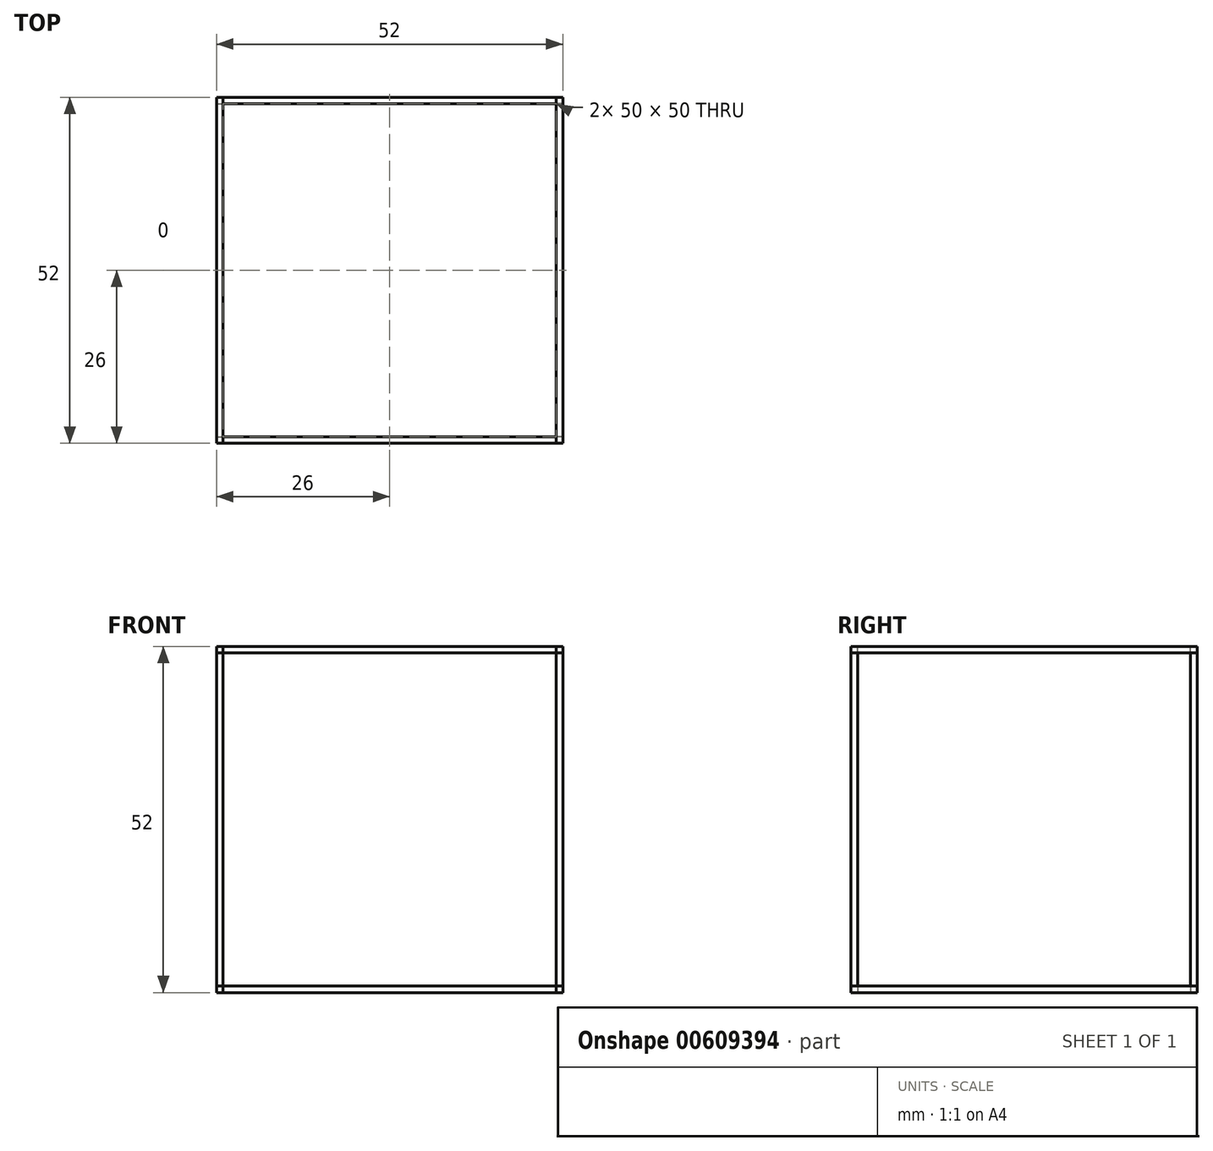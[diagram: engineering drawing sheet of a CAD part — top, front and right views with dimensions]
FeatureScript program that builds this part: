
annotation { "Feature Type Name" : "Feature", "Feature Type Description" : "" }
export const myFeature = defineFeature(function(context is Context, id is Id, definition is map)
    precondition{}
    {
        {
            var Q0;
            Q0=qCreatedBy(makeId("Top.planeOp"),FACE);
            var sketch = newSketch(context, id + "F0", { "sketchPlane" : qUnion([Q0])});
            skLineSegment(sketch, "E0.bottom", {"start": v(25, -25) * mm, "end": v(-25, -25) * mm});
            skLineSegment(sketch, "E0.top", {"start": v(25, 25) * mm, "end": v(-25, 25) * mm});
            skLineSegment(sketch, "E0.left", {"start": v(25, -25) * mm, "end": v(25, 25) * mm});
            skLineSegment(sketch, "E0.right", {"start": v(-25, -25) * mm, "end": v(-25, 25) * mm});
            skPoint(sketch, "E0.middle", {"position": v(0, 0) * mm});
            skLineSegment(sketch, "E1.0", {"start": v(26, 26) * mm, "end": v(-26, 26) * mm});
            skLineSegment(sketch, "E1.1", {"start": v(26, -26) * mm, "end": v(26, 26) * mm});
            skLineSegment(sketch, "E1.2", {"start": v(26, -26) * mm, "end": v(-26, -26) * mm});
            skLineSegment(sketch, "E1.3", {"start": v(-26, -26) * mm, "end": v(-26, 26) * mm});
            skSolve(sketch);
        }
        {
            var Q0;
            Q0 = qSketchRegion(id + "F0", true);
            extrude(context, id + "F1", {"entities" : qUnion([Q0]), "depth" : 1 * mm, "offsetDistance" : 25 * mm});
        }
        {
            var Q0;
            Q0=makeQuery(id+"F1.opExtrude","SWEPT_BODY",BODY,{"disambiguationData":[OSD([sQuery(id+"F0.wireOp",EDGE,"E0.bottom"),sQuery(id+"F0.wireOp",EDGE,"E0.top"),sQuery(id+"F0.wireOp",EDGE,"E0.left"),sQuery(id+"F0.wireOp",EDGE,"E0.right"),sQuery(id+"F0.wireOp",EDGE,"E1.0"),sQuery(id+"F0.wireOp",EDGE,"E1.1"),sQuery(id+"F0.wireOp",EDGE,"E1.2"),sQuery(id+"F0.wireOp",EDGE,"E1.3")])]});
            var Q1;
            Q1=makeQuery(id+"F1.opExtrude","CAP_EDGE",EDGE,{"disambiguationData":[OSD([sQuery(id+"F0.wireOp",EDGE,"E1.3")])],"isStart":false});
            transform(context, id + "F2", {"entities" : qUnion([Q0]), "transformType" : TransformType.ROTATION, "transformAxis" : qUnion([Q1]), "angle" : 90 * degree, "oppositeDirection" : true, "makeCopy" : true});
        }
        {
            var Q0;
            Q0=makeQuery(id+"F2.opPattern","COPY",BODY,{"derivedFrom":makeQuery(id+"F1.opExtrude","SWEPT_BODY",BODY,{"disambiguationData":[OSD([sQuery(id+"F0.wireOp",EDGE,"E0.bottom"),sQuery(id+"F0.wireOp",EDGE,"E0.top"),sQuery(id+"F0.wireOp",EDGE,"E0.left"),sQuery(id+"F0.wireOp",EDGE,"E0.right"),sQuery(id+"F0.wireOp",EDGE,"E1.0"),sQuery(id+"F0.wireOp",EDGE,"E1.1"),sQuery(id+"F0.wireOp",EDGE,"E1.2"),sQuery(id+"F0.wireOp",EDGE,"E1.3")])]}),"instanceName":"1"});
            var Q1;
            Q1=makeQuery(id+"F2.opPattern","COPY",EDGE,{"derivedFrom":makeQuery(id+"F1.opExtrude","CAP_EDGE",EDGE,{"disambiguationData":[OSD([sQuery(id+"F0.wireOp",EDGE,"E1.1")])],"isStart":false}),"instanceName":"1"});
            transform(context, id + "F3", {"entities" : qUnion([Q0]), "transformType" : TransformType.ROTATION, "transformAxis" : qUnion([Q1]), "angle" : 90 * degree, "oppositeDirection" : true, "makeCopy" : true});
        }
        {
            var Q0;
            Q0=makeQuery(id+"F3.opPattern","COPY",BODY,{"derivedFrom":makeQuery(id+"F2.opPattern","COPY",BODY,{"derivedFrom":makeQuery(id+"F1.opExtrude","SWEPT_BODY",BODY,{"disambiguationData":[OSD([sQuery(id+"F0.wireOp",EDGE,"E0.bottom"),sQuery(id+"F0.wireOp",EDGE,"E0.top"),sQuery(id+"F0.wireOp",EDGE,"E0.left"),sQuery(id+"F0.wireOp",EDGE,"E0.right"),sQuery(id+"F0.wireOp",EDGE,"E1.0"),sQuery(id+"F0.wireOp",EDGE,"E1.1"),sQuery(id+"F0.wireOp",EDGE,"E1.2"),sQuery(id+"F0.wireOp",EDGE,"E1.3")])]}),"instanceName":"1"}),"instanceName":"1"});
            var Q1;
            Q1=makeQuery(id+"F3.opPattern","COPY",EDGE,{"derivedFrom":makeQuery(id+"F2.opPattern","COPY",EDGE,{"derivedFrom":makeQuery(id+"F1.opExtrude","CAP_EDGE",EDGE,{"disambiguationData":[OSD([sQuery(id+"F0.wireOp",EDGE,"E1.3")])],"isStart":false}),"instanceName":"1"}),"instanceName":"1"});
            transform(context, id + "F4", {"entities" : qUnion([Q0]), "transformType" : TransformType.ROTATION, "transformAxis" : qUnion([Q1]), "angle" : 90 * degree, "oppositeDirection" : true, "makeCopy" : true});
        }
        {
            var Q0;
            Q0=makeQuery(id+"F1.opExtrude","SWEPT_BODY",BODY,{"disambiguationData":[OSD([sQuery(id+"F0.wireOp",EDGE,"E0.bottom"),sQuery(id+"F0.wireOp",EDGE,"E0.top"),sQuery(id+"F0.wireOp",EDGE,"E0.left"),sQuery(id+"F0.wireOp",EDGE,"E0.right"),sQuery(id+"F0.wireOp",EDGE,"E1.0"),sQuery(id+"F0.wireOp",EDGE,"E1.1"),sQuery(id+"F0.wireOp",EDGE,"E1.2"),sQuery(id+"F0.wireOp",EDGE,"E1.3")])]});
            transform(context, id + "F5", {"entities" : qUnion([Q0]), "transformType" : TransformType.TRANSLATION_3D, "dx" : 0 * mm, "dy" : 0 * mm, "dz" : 1 * mm, "makeCopy" : false});
        }
        {
            var Q0;
            Q0=makeQuery(id+"F3.opPattern","COPY",BODY,{"derivedFrom":makeQuery(id+"F2.opPattern","COPY",BODY,{"derivedFrom":makeQuery(id+"F1.opExtrude","SWEPT_BODY",BODY,{"disambiguationData":[OSD([sQuery(id+"F0.wireOp",EDGE,"E0.bottom"),sQuery(id+"F0.wireOp",EDGE,"E0.top"),sQuery(id+"F0.wireOp",EDGE,"E0.left"),sQuery(id+"F0.wireOp",EDGE,"E0.right"),sQuery(id+"F0.wireOp",EDGE,"E1.0"),sQuery(id+"F0.wireOp",EDGE,"E1.1"),sQuery(id+"F0.wireOp",EDGE,"E1.2"),sQuery(id+"F0.wireOp",EDGE,"E1.3")])]}),"instanceName":"1"}),"instanceName":"1"});
            transform(context, id + "F6", {"entities" : qUnion([Q0]), "transformType" : TransformType.TRANSLATION_3D, "dx" : 0 * mm, "dy" : 0 * mm, "dz" : -1 * mm, "makeCopy" : false});
        }
    });
